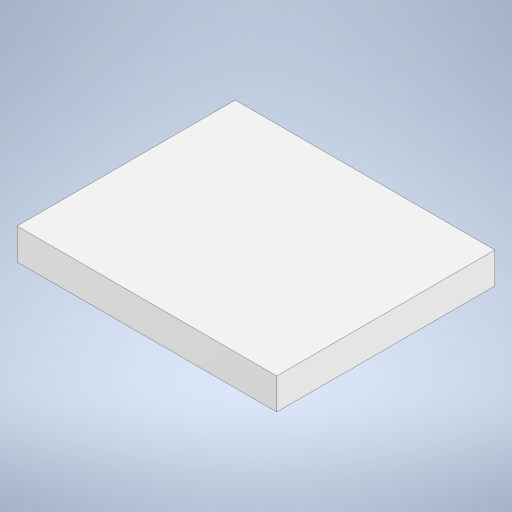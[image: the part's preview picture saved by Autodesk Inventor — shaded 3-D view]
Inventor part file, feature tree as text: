
AUTODESK INVENTOR PART (.ipt)
format: ipt  version: 2023 (Build 270158000, 158)  size: 196,096 bytes
history: native  units: in
note: dims shown in document units (in); Inventor stores cm internally (conversion verified against a paired STEP export)
features: extrude x1, sketch x1
ambient origin geometry x8: Origin, YZ Plane, XZ Plane, XY Plane, X Axis, Y Axis, Z Axis, Center Point
bodies: Solid1 (feature_tree)
feature tree (2):
  extrude  "Extrusion1"  Depth=2.1in
  sketch  "Sketch1"  dims[d0=2.5in d1=2.1in d2=0.3in d3=0.0in]
